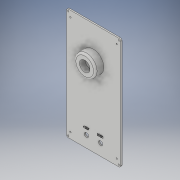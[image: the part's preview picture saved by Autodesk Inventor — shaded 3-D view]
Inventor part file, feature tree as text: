
AUTODESK INVENTOR PART (.ipt)
format: ipt  version: 2019 (Build 230136000, 136)  size: 334,848 bytes
history: native  units: in
note: dims shown in document units (in); Inventor stores cm internally (conversion verified against a paired STEP export)
features: sketch x6, extrude x3, hole x3, other x2, fillet x1, imported_body x1
ambient origin geometry x8: Origin, YZ Plane, XZ Plane, XY Plane, X Axis, Y Axis, Z Axis, Center Point
bodies: Solid1 (feature_tree)
feature tree (16):
  other  "InnerDoorCover"
  extrude  "Extrusion1"  Depth=7.87in
  hole  "ScrewHoles"  [1 undecoded]
  hole  "InputHoles"  [1 undecoded]
  extrude  "ButtonStand"  Depth=0.13in
  hole  "ButtonHole"  [1 undecoded]
  fillet  "Fillet1"  Radius=0.13in
  other  "Text"
  extrude  "ButtonSink"  Depth=0.3in
  imported_body  "Base"
  sketch  "Sketch2"  dims[d0=3.83in d1=7.87in]
  sketch  "Sketch3"  dims[d2=0.125in d3=0.1in d4=0.0in]
  sketch  "Sketch4"  dims[d5=0.13in d6=0.13in]
  sketch  "Sketch5"  dims[d7=0.13in d8=0.13in]
  sketch  "Sketch6"  dims[d9=0.13in d10=0.13in d11=0.13in]
  sketch  "Sketch7"  dims[d12=0.13in d13=0.43in d14=0.28in d15=0.28in d16=0.43in d17=0.43in d18=0.28in d19=0.43in d20=0.28in d21=0.1in d22=0.75in d23=0.375in d24=0.25in d25=0.5635in d26=0.1in d27=0.8108in d30=0.305in d31=0.75in d32=0.375in d33=0.25in d34=0.5635in d35=0.1in d36=0.8108in d37=1.5in d38=0.6in d39=0.0in d40=0.744in d41=0.75in d42=0.375in d43=0.25in d44=0.5635in d45=0.1in d46=0.8108in d47=0.125in d48=0.05in d49=0.0in d50=1.1in d51=0.3in d52=0.0in d28=0.75in d29=0.8108in]
note: 3 required parameter values undecoded (feature->parameter linkage not recoverable at this tier; creation-order binding heuristic only, values carry confidence <= 0.55)
